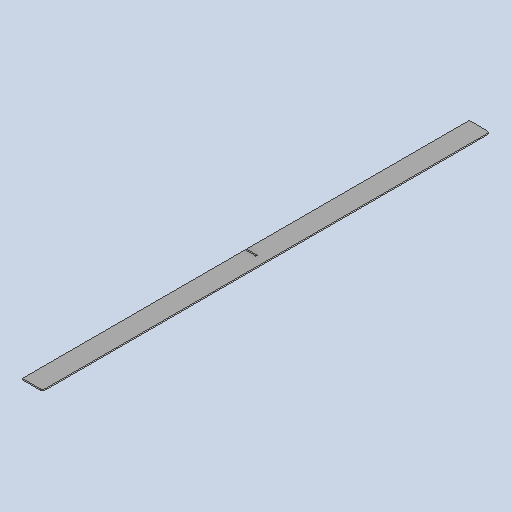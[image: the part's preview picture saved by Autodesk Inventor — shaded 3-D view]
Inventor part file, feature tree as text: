
AUTODESK INVENTOR PART (.ipt)
format: ipt  version: 2025 (Build 290162010, 162A)  size: 294,912 bytes
history: native  units: mm
features: other x3, sheet_metal_op x1, chamfer x1, sketch x1
ambient origin geometry x8: Origin, YZ Plane, XZ Plane, XY Plane, X Axis, Y Axis, Z Axis, Center Point
bodies: Body1 (feature_tree)
feature tree (6):
  other  "BSH 506 amplifier"
  sheet_metal_op  "Face2"
  chamfer  "Corner Round2"
  sketch  "Sketch1"  dims[d15=3.0mm d17=1098.0mm d18=50.0mm d19=3.0mm d20=26.0mm d22=6.0mm]
  other  "Plate2"
  other  "Definition1"
